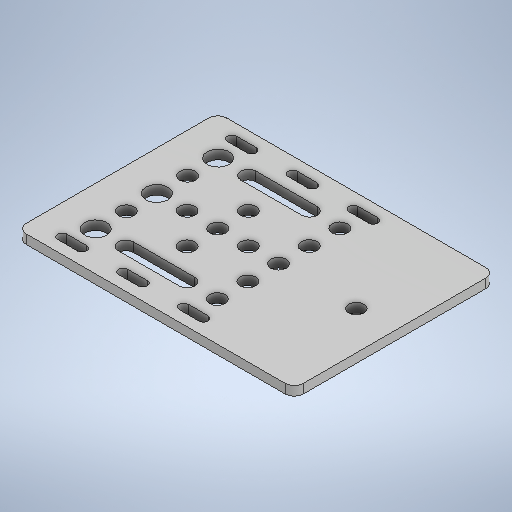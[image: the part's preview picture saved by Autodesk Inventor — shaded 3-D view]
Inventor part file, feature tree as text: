
AUTODESK INVENTOR PART (.ipt)
format: ipt  version: 2025.2 (Build 292293000, 293)  size: 348,672 bytes
history: native  units: in
note: dims shown in document units (in); Inventor stores cm internally (conversion verified against a paired STEP export)
features: extrude x1, fillet x1, sketch x1
ambient origin geometry x8: Origin, YZ Plane, XZ Plane, XY Plane, X Axis, Y Axis, Z Axis, Center Point
bodies: Solid1 (feature_tree), Body1 (feature_tree)
feature tree (3):
  extrude  "Extrusion1"  Depth=0.1969in
  fillet  "Fillet1"  Radius=0.1181in
  sketch  "Sketch1"  dims[d5=0.9843in d6=0.1969in d7=0.1181in d8=0.0in d9=0.1181in]
